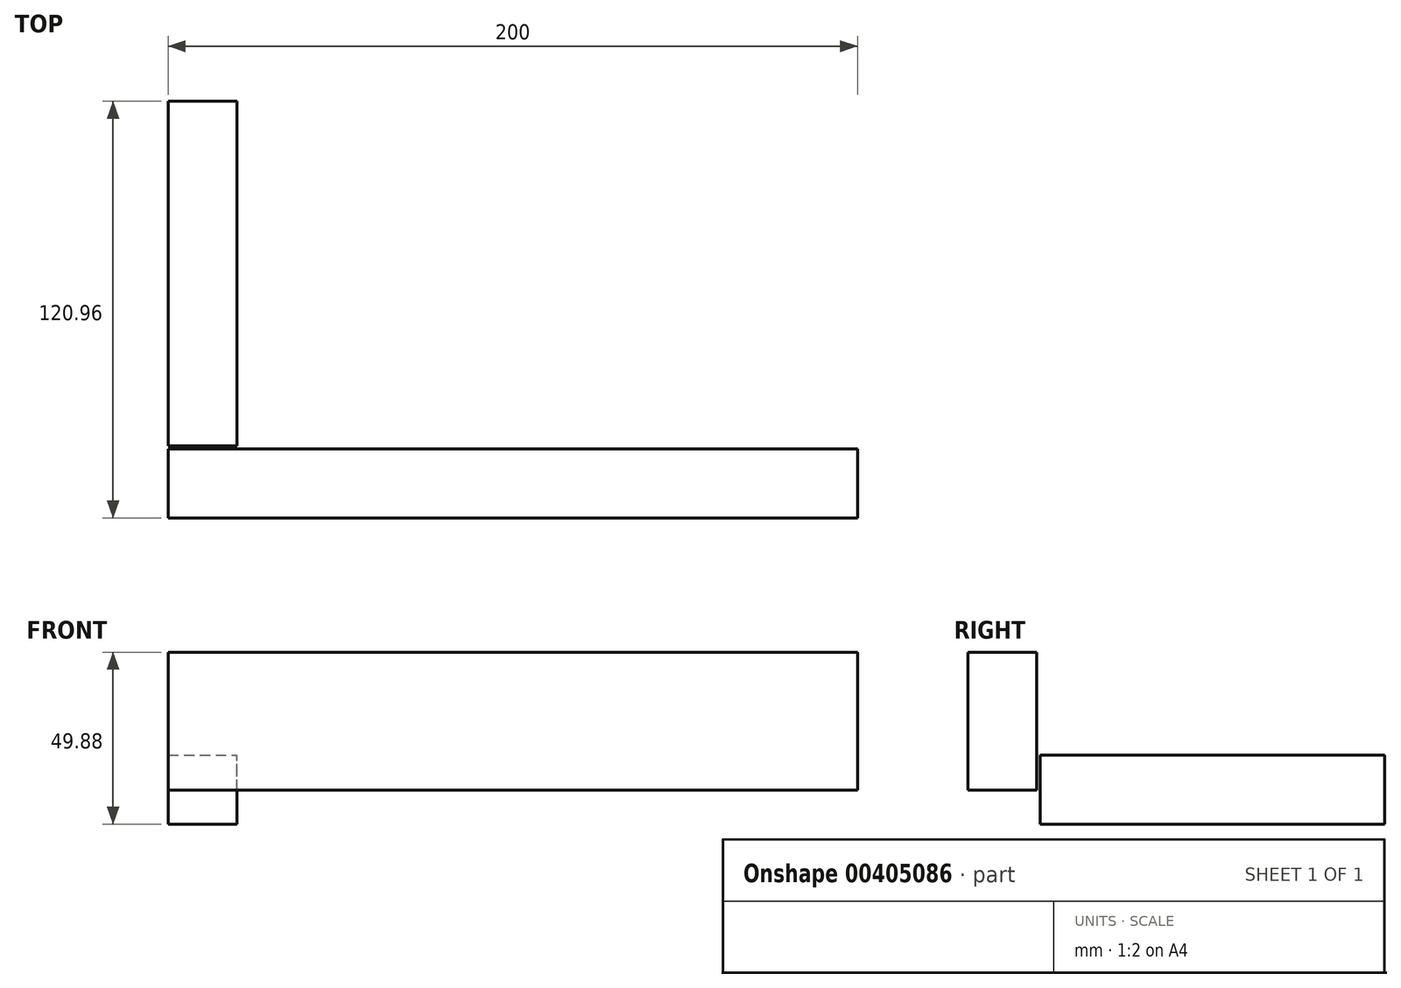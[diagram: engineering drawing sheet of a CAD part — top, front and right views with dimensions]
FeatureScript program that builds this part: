
annotation { "Feature Type Name" : "Feature", "Feature Type Description" : "" }
export const myFeature = defineFeature(function(context is Context, id is Id, definition is map)
    precondition{}
    {
        {
            var Q0;
            Q0=qCreatedBy(makeId("Front.planeOp"),FACE);
            var sketch = newSketch(context, id + "F0", { "sketchPlane" : qUnion([Q0])});
            skLineSegment(sketch, "E0.bottom", {"start": v(0, 0) * mm, "end": v(20, 0) * mm});
            skLineSegment(sketch, "E0.top", {"start": v(0, 20) * mm, "end": v(20, 20) * mm});
            skLineSegment(sketch, "E0.left", {"start": v(0, 0) * mm, "end": v(0, 20) * mm});
            skLineSegment(sketch, "E0.right", {"start": v(20, 0) * mm, "end": v(20, 20) * mm});
            skSolve(sketch);
        }
        {
            var Q0;
            Q0 = qSketchRegion(id + "F0", true);
            extrude(context, id + "F1", {"entities" : qUnion([Q0]), "depth" : 100 * mm});
        }
        {
            var Q0;
            Q0=qCreatedBy(makeId("Right.planeOp"),FACE);
            var sketch = newSketch(context, id + "F2", { "sketchPlane" : qUnion([Q0])});
            skLineSegment(sketch, "E1.bottom", {"start": v(-120.96, 9.88) * mm, "end": v(-100.96, 9.88) * mm});
            skLineSegment(sketch, "E1.top", {"start": v(-120.96, 49.88) * mm, "end": v(-100.96, 49.88) * mm});
            skLineSegment(sketch, "E1.left", {"start": v(-120.96, 9.88) * mm, "end": v(-120.96, 49.88) * mm});
            skLineSegment(sketch, "E1.right", {"start": v(-100.96, 9.88) * mm, "end": v(-100.96, 49.88) * mm});
            skSolve(sketch);
        }
        {
            var Q0;
            Q0=makeQuery(id+"F2.imprint","IMPRINT",FACE,{"disambiguationData":[TD([[makeQuery(id+"F2.imprint","IMPRINT",EDGE,{"derivedFrom":sQuery(id+"F2.wireOp",EDGE,"E1.bottom")}),1.0]])]});
            extrude(context, id + "F3", {"entities" : qUnion([Q0]), "depth" : 200 * mm});
        }
    });
